# Revit family: PCHA COMBO
name_source: partatom
category: Lighting Fixtures
units: mm (PartAtom-declared; Revit-internal decimal feet)

## family parameters
Cut with Voids When Loaded = No
Host = Face
Light Source = Yes
Maintain Annotation Orientation = No
Part Type = Normal
Room Calculation Point = No
Round Connector Dimension = Use Diameter
Shared = No

## types (2) — shared parameters
Color Filter = 16777215
Default Elevation = 4' - 0"
Dimming Lamp Color Temperature Shift = <None>
Emit from Line Length = 2' - 0"
FACE MATERIAL = FACE MATERIAL
HOUSING MATERIAL = HOUSING MATERIAL
LENS MATERIAL = LENS MATERIAL
LETTER MATERIAL = LETTER MATERIAL GREEN
Lamp = LED
Manufacturer = BEGHELLI
Model = PCHAC
SCREW MATERIAL = SCREWS MATERIAL
Type Comments = EM SIGN COMBO
Type Image = PCHAC - IMAGE.jpg
Wattage Comments = 2W

## per-type parameters (varying)
| type | Photometric Web File | Tilt Angle |
| PCHAC-G | generic | 60.00° |
| PCHAC-R | PCHAC-IES.ies | -90.00° |

## geometry (parser evidence)
native form markers: Sweep x15
no freeform markers — native parametric forms only
